# Revit family: Ulimax_Aluminio_Porta-de-Giro-1-Folha-Vidro
name_source: partatom
category: Portas
units: mm (PartAtom-declared; Revit-internal decimal feet)

## family parameters
Compartilhado = Não
Corte com vazios quando carregada = Não
Hospedeiro = Parede
Número OmniClass = 23.30.10.00
Ponto de cálculo do ambiente = Não
Sempre na vertical = Sim
Título OmniClass = Doors

## types (16) — shared parameters
Altura = 210
Altura Maçaneta = 110
Altura bruta = 219.14
Comentários de tipos = Porta de Giro Skyfull
Construção analítica = <Nenhum>
Definir propriedades térmicas por = Tipo esquemático
Descrição = Porta com esquadria minimalista de alumínio e vidro, 1 Folha
Developer = Blocks
Espessura = 5
Fabricante = Ulimax - Wood & Aluminum
Fechamento da parede = Por hospedeiro
URL = https://www.ulimax.com.br
URL Developer = https://BlocksRvt.com
URL Produto = https://www.ulimax.com.br
URL Template = https://www.ulimax.com.br
Visor = Ulimax - Glass - Transparent

## per-type parameters (varying)
| type | Batente | Caixilho | Largura | Largura bruta | Puxador |
| Branco - 0.70 x 2.10 | Ulimax - Metal - White - Matte - 246-246-243 | Ulimax - Metal - White - Matte - 246-246-243 | 70 | 79.14 | Ulimax - Metal - White - Matte - 246-246-243 |
| Cinza - 0.60 x 2.10 | Ulimax - Metal - Chrome - 203-203-203 | Ulimax - Metal - Chrome - 203-203-203 | 60 | 69.14 | Ulimax - Metal - Chrome - 203-203-203 |
| Cinza - 0.80 x 2.10 | Ulimax - Metal - Chrome - 203-203-203 | Ulimax - Metal - Chrome - 203-203-203 | 80 | 89.14 | Ulimax - Metal - Chrome - 203-203-203 |
| Branco - 0.90 x 2.10 | Ulimax - Metal - White - Matte - 246-246-243 | Ulimax - Metal - White - Matte - 246-246-243 | 90 | 99.14 | Ulimax - Metal - White - Matte - 246-246-243 |
| Preto - 0.70 x 2.10 | Ulimax - Metal - Black - Matte - 15-15-15 | Ulimax - Metal - Black - Matte - 15-15-15 | 70 | 79.14 | Ulimax - Metal - Black - Matte - 15-15-15 |
| Preto - 0.80 x 2.10 | Ulimax - Metal - Black - Matte - 15-15-15 | Ulimax - Metal - Black - Matte - 15-15-15 | 80 | 89.14 | Ulimax - Metal - Black - Matte - 15-15-15 |
| Preto - 0.90 x 2.10 | Ulimax - Metal - Black - Matte - 15-15-15 | Ulimax - Metal - Black - Matte - 15-15-15 | 90 | 99.14 | Ulimax - Metal - Black - Matte - 15-15-15 |
| Preto - 0.60 x 2.10 | Ulimax - Metal - Black - Matte - 15-15-15 | Ulimax - Metal - Black - Matte - 15-15-15 | 60 | 69.14 | Ulimax - Metal - Black - Matte - 15-15-15 |
| Branco - 0.60 x 2.10 | Ulimax - Metal - White - Matte - 246-246-243 | Ulimax - Metal - White - Matte - 246-246-243 | 60 | 69.14 | Ulimax - Metal - White - Matte - 246-246-243 |
| Cinza - 0.70 x 2.10 | Ulimax - Metal - Chrome - 203-203-203 | Ulimax - Metal - Chrome - 203-203-203 | 70 | 79.14 | Ulimax - Metal - Chrome - 203-203-203 |
| Branco - 0.80 x 2.10 | Ulimax - Metal - White - Matte - 246-246-243 | Ulimax - Metal - White - Matte - 246-246-243 | 80 | 89.14 | Ulimax - Metal - White - Matte - 246-246-243 |
| Champanhe - 0.60 x 2.10 | Ulimax - Metal - Beige - Matte - 230-200-160 | Ulimax - Metal - Beige - Matte - 230-200-160 | 60 | 69.14 | Ulimax - Metal - Beige - Matte - 230-200-160 |
| Champanhe - 0.70 x 2.10 | Ulimax - Metal - Beige - Matte - 230-200-160 | Ulimax - Metal - Beige - Matte - 230-200-160 | 70 | 79.14 | Ulimax - Metal - Beige - Matte - 230-200-160 |
| Champanhe - 0.80 x 2.10 | Ulimax - Metal - Beige - Matte - 230-200-160 | Ulimax - Metal - Beige - Matte - 230-200-160 | 80 | 89.14 | Ulimax - Metal - Beige - Matte - 230-200-160 |
| Champanhe - 0.90 x 2.10 | Ulimax - Metal - Beige - Matte - 230-200-160 | Ulimax - Metal - Beige - Matte - 230-200-160 | 90 | 99.14 | Ulimax - Metal - Beige - Matte - 230-200-160 |
| Cinza - 0.90 x 2.10 | Ulimax - Metal - Chrome - 203-203-203 | Ulimax - Metal - Chrome - 203-203-203 | 90 | 99.14 | Ulimax - Metal - Chrome - 203-203-203 |
